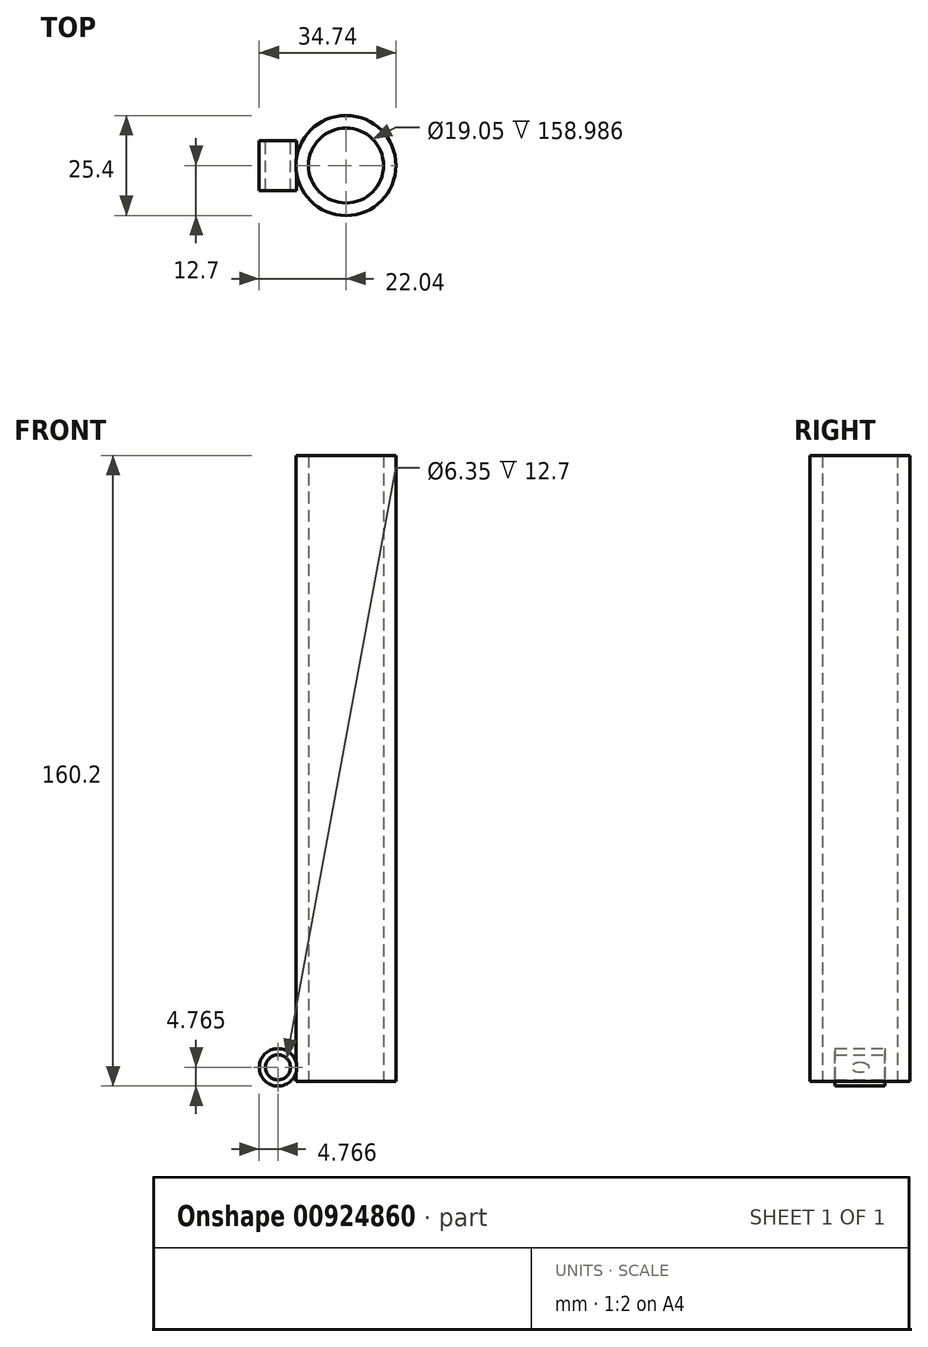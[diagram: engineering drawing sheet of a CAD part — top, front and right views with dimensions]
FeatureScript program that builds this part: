
annotation { "Feature Type Name" : "Feature", "Feature Type Description" : "" }
export const myFeature = defineFeature(function(context is Context, id is Id, definition is map)
    precondition{}
    {
        {
            var Q0;
            Q0=qCreatedBy(makeId("Top.planeOp"),FACE);
            var sketch = newSketch(context, id + "F0", { "sketchPlane" : qUnion([Q0])});
            skCircle(sketch, "E0", {"center": v(0, 0) * mm, "radius": 12.7 * mm});
            skCircle(sketch, "E1", {"center": v(0, 0) * mm, "radius": 9.53 * mm});
            skSolve(sketch);
        }
        {
            var Q0;
            Q0 = qSketchRegion(id + "F0", true);
            extrude(context, id + "F1", {"entities" : qUnion([Q0]), "depth" : 159 * mm, "offsetDistance" : 25.4 * mm});
        }
        {
            var Q0;
            Q0=qCreatedBy(makeId("Front.planeOp"),FACE);
            var sketch = newSketch(context, id + "F2", { "sketchPlane" : qUnion([Q0])});
            skCircle(sketch, "E2", {"center": v(-17.27, 3.55) * mm, "radius": 4.76 * mm});
            skCircle(sketch, "E3", {"center": v(-17.27, 3.55) * mm, "radius": 3.18 * mm});
            skSolve(sketch);
        }
        {
            var Q0;
            Q0=makeQuery(id+"F2.imprint","IMPRINT",FACE,{"disambiguationData":[TD([[makeQuery(id+"F2.imprint","IMPRINT",EDGE,{"derivedFrom":sQuery(id+"F2.wireOp",EDGE,"E2")}),1.0]])]});
            extrude(context, id + "F3", {"entities" : qUnion([Q0]), "operationType" : NewBodyOperationType.ADD, "depth" : 6.35 * mm, "offsetDistance" : 25.4 * mm, "hasSecondDirection" : true, "secondDirectionOppositeDirection" : true, "secondDirectionDepth" : 6.35 * mm});
        }
    });
